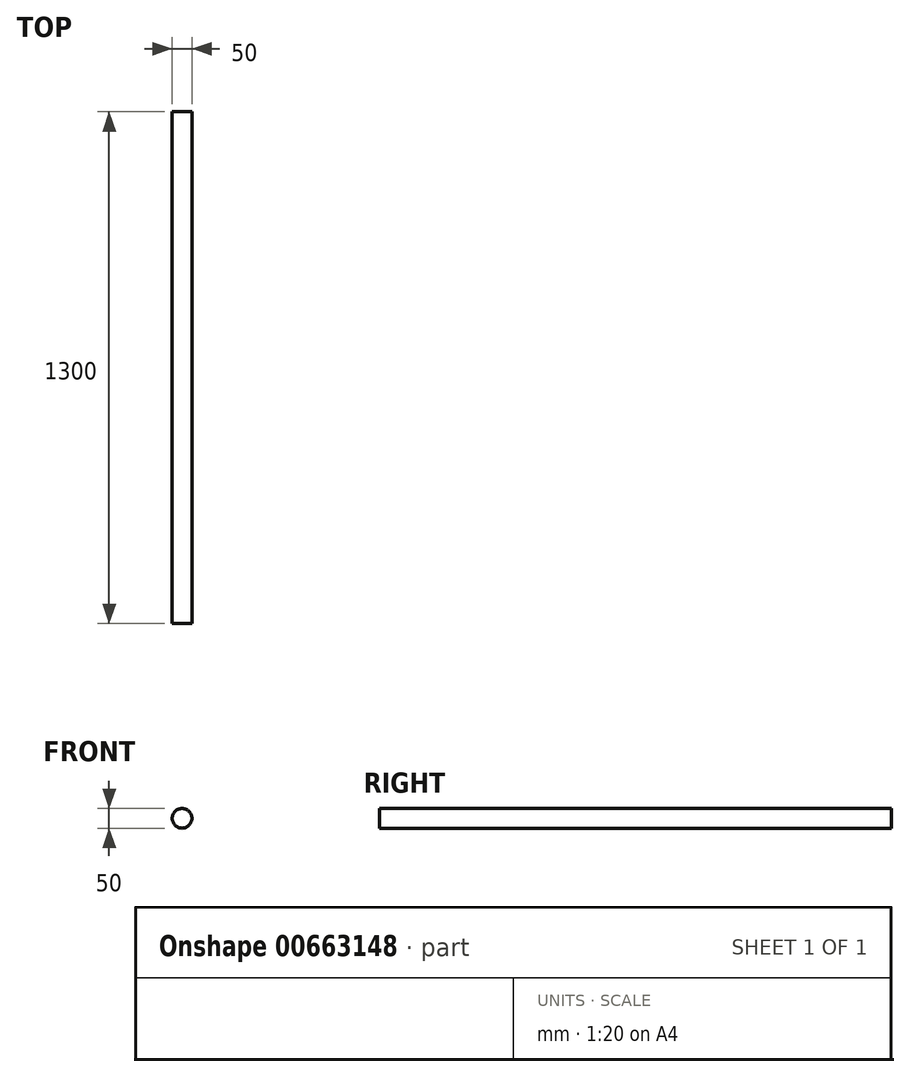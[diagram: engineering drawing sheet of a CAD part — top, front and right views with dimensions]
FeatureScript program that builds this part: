
annotation { "Feature Type Name" : "Feature", "Feature Type Description" : "" }
export const myFeature = defineFeature(function(context is Context, id is Id, definition is map)
    precondition{}
    {
        {
            var Q0;
            Q0=qCreatedBy(makeId("Front.planeOp"),FACE);
            var sketch = newSketch(context, id + "F0", { "sketchPlane" : qUnion([Q0])});
            skCircle(sketch, "E0", {"center": v(0, 0) * mm, "radius": 25 * mm});
            skSolve(sketch);
        }
        {
            var Q0;
            Q0 = qSketchRegion(id + "F0", true);
            extrude(context, id + "F1", {"entities" : qUnion([Q0]), "depth" : 1300 * mm, "offsetDistance" : 25 * mm});
        }
    });
